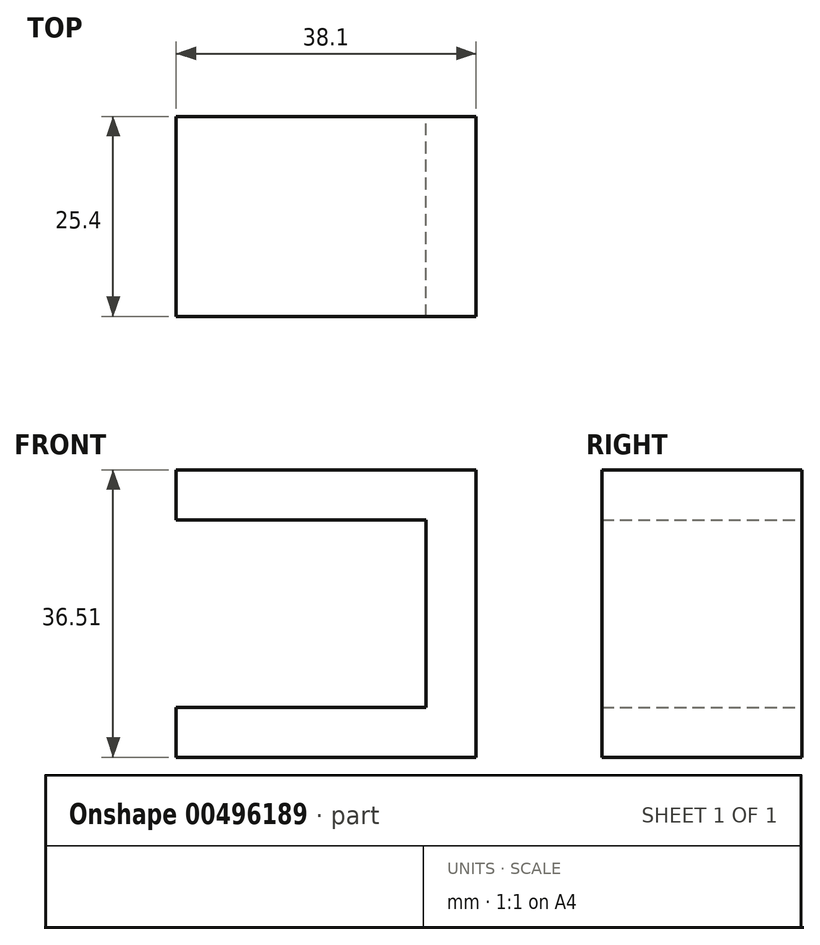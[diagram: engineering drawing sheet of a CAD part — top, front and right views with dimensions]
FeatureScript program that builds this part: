
annotation { "Feature Type Name" : "Feature", "Feature Type Description" : "" }
export const myFeature = defineFeature(function(context is Context, id is Id, definition is map)
    precondition{}
    {
        {
            var Q0;
            Q0=qCreatedBy(makeId("Front.planeOp"),FACE);
            var sketch = newSketch(context, id + "F0", { "sketchPlane" : qUnion([Q0])});
            skLineSegment(sketch, "E0", {"start": v(0, 36.51) * mm, "end": v(38.1, 36.51) * mm});
            skLineSegment(sketch, "E1", {"start": v(38.1, 36.51) * mm, "end": v(38.1, 0) * mm});
            skLineSegment(sketch, "E2", {"start": v(38.1, 0) * mm, "end": v(0, 0) * mm});
            skLineSegment(sketch, "E3", {"start": v(0, 36.51) * mm, "end": v(0, 30.16) * mm});
            skLineSegment(sketch, "E4", {"start": v(0, 30.16) * mm, "end": v(31.75, 30.16) * mm});
            skLineSegment(sketch, "E5", {"start": v(0, 0) * mm, "end": v(0, 6.35) * mm});
            skLineSegment(sketch, "E6", {"start": v(0, 6.35) * mm, "end": v(31.75, 6.35) * mm});
            skLineSegment(sketch, "E7", {"start": v(31.75, 30.16) * mm, "end": v(31.75, 6.35) * mm});
            skSolve(sketch);
        }
        {
            var Q0;
            Q0=makeQuery(id+"F0.imprint","IMPRINT",FACE,{"disambiguationData":[TD([[makeQuery(id+"F0.imprint","IMPRINT",EDGE,{"derivedFrom":sQuery(id+"F0.wireOp",EDGE,"E0")}),-1.0]])]});
            extrude(context, id + "F1", {"entities" : qUnion([Q0]), "depth" : 25.4 * mm});
        }
    });
